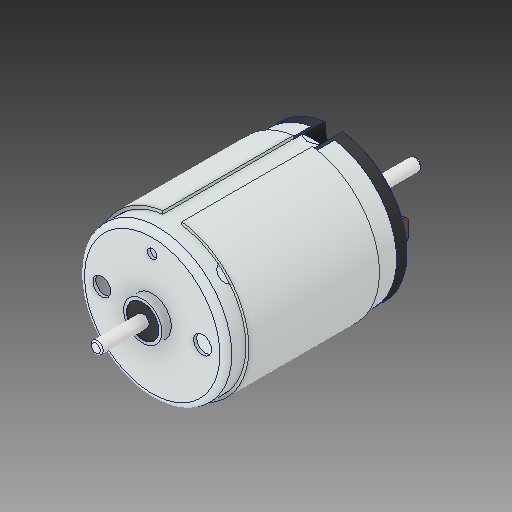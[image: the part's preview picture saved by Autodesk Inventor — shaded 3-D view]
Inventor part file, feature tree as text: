
AUTODESK INVENTOR PART (.ipt)
format: ipt  version: 2019 (Build 230136000, 136)  size: 345,088 bytes
history: mixed  units: mm
features: other x5, fillet x3, imported_body x1
ambient origin geometry x8: Origin, YZ Plane, XZ Plane, XY Plane, X Axis, Y Axis, Z Axis, Center Point
bodies: Body1 (imported_parasolid), Body2 (imported_parasolid), Body3 (imported_parasolid), Body4 (imported_parasolid)
feature tree (9):
  other  "Твердое тело1"
  other  "Твердое тело2"
  other  "Твердое тело3"
  other  "Твердое тело4"
  other  "Cut-Extrude8"
  fillet  "Fillet5"  [1 undecoded]
  fillet  "Fillet6"  [1 undecoded]
  fillet  "Fillet7"  [1 undecoded]
  imported_body  NMx_Import_Brep_tag  [imported B-rep: ~49 faces, bbox_mm=[20.9, 14.800391, 54.0]]
note: 3 required parameter values undecoded (feature->parameter linkage not recoverable at this tier; creation-order binding heuristic only, values carry confidence <= 0.55)
